# Revit family: NGC_55_19W_4000K_1766LM
name_source: partatom
category: Lighting Fixtures
units: mm (PartAtom-declared; Revit-internal decimal feet)

## family parameters
Always vertical = Yes
Cut with Voids When Loaded = No
Host = Ceiling
Light Source = Yes
OmniClass Number = 23.80.70.11
OmniClass Title = Luminaries for Internal Lighting
Part Type = Normal
Room Calculation Point = No
Round Connector Dimension = Use Diameter
Shared = No

## types (1)
- Type 1
    Alimentation Driver = AC 220-240V
    Alimentation luminaire = 25-40V dc / 500mA
    Angle d'éclairage = 50°
    Color Filter = 16777215
    Couleur = Blanc
    Default Elevation = 0 mm  [stored 0 ft]
    Dimension découpe = 195 x 45 mm
    Dimensions = 205 x 55 mm, H = 50 mm
    Dimming Lamp Color Temperature Shift = <None>
    Driver = Driver Lifud TUV CE CCC
    Durée de vie = 50 000 heures
    Emit Shape Visible in Rendering = No
    Emit from Rectangle Length = 1219 mm
    Emit from Rectangle Width = 610 mm
    IRC = >90
    Maintien du flux = L80B10 (50 000 heures)
    Matériau = Aluminium
    Photometric Web File = google_eulumdat_converter (19).ies
    Puissance nominale = 19.5W
    Tilt Angle = 90.00°
    Type = Downlight
    Type de lampe = LED TYF-5050 Bridgelux 2240

note: [stored X ft] marks values corroborated as IEEE doubles in the binary element streams (Revit-internal decimal feet)
